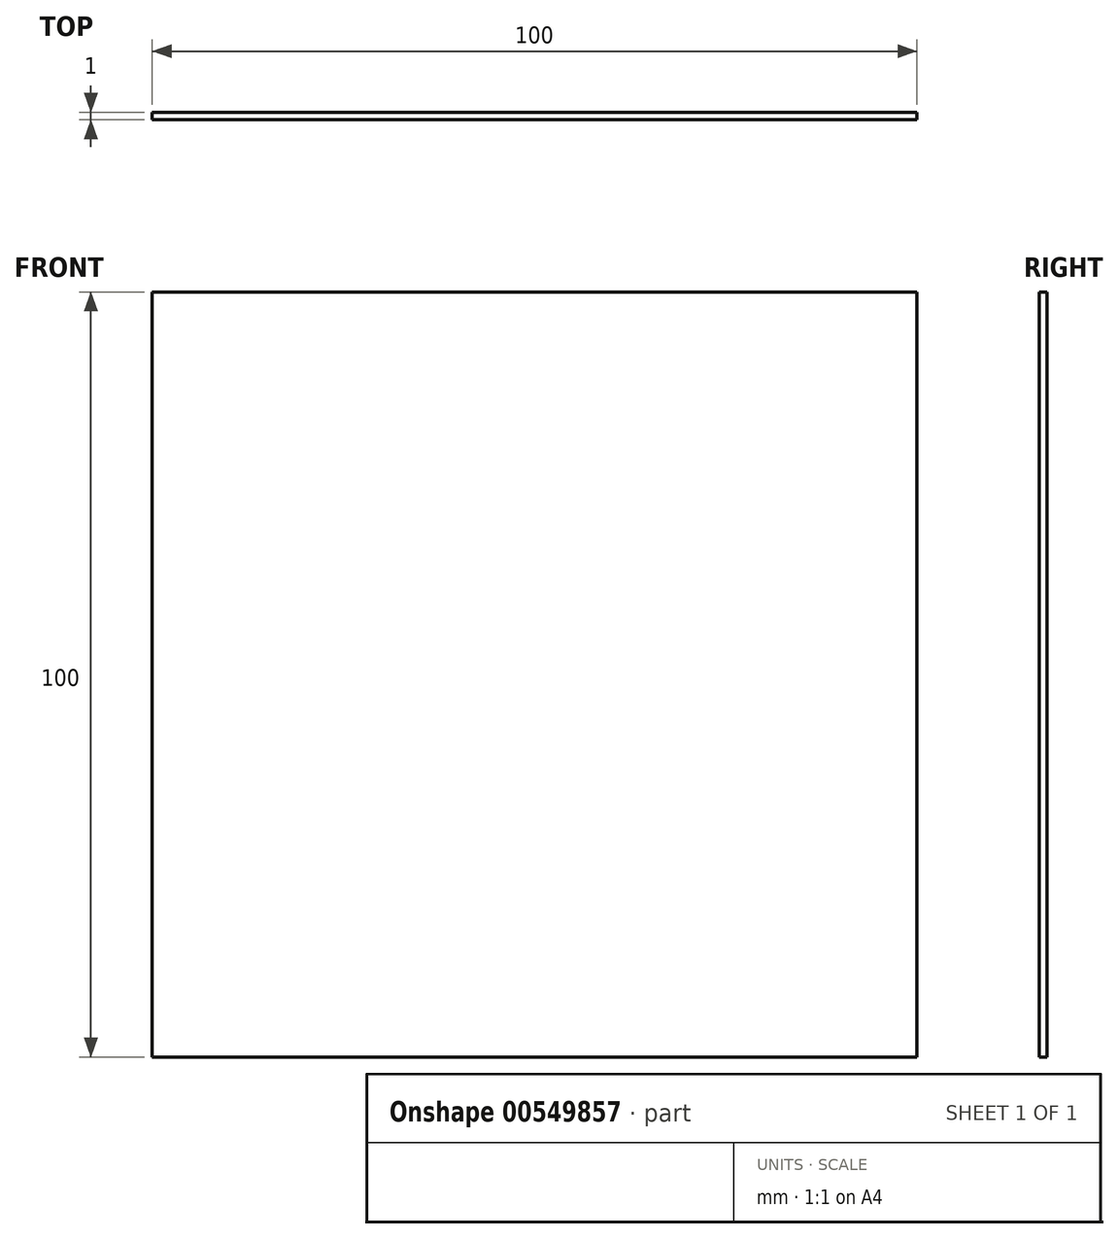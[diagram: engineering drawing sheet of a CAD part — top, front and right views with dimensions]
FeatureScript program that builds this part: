
annotation { "Feature Type Name" : "Feature", "Feature Type Description" : "" }
export const myFeature = defineFeature(function(context is Context, id is Id, definition is map)
    precondition{}
    {
        {
            var Q0;
            Q0=qCreatedBy(makeId("Front.planeOp"),FACE);
            var sketch = newSketch(context, id + "F0", { "sketchPlane" : qUnion([Q0])});
            skLineSegment(sketch, "E0.bottom", {"start": v(0, 0) * mm, "end": v(100, 0) * mm});
            skLineSegment(sketch, "E0.top", {"start": v(0, 100) * mm, "end": v(100, 100) * mm});
            skLineSegment(sketch, "E0.left", {"start": v(0, 0) * mm, "end": v(0, 100) * mm});
            skLineSegment(sketch, "E0.right", {"start": v(100, 0) * mm, "end": v(100, 100) * mm});
            skSolve(sketch);
        }
        {
            var Q0;
            Q0=makeQuery(id+"F0.imprint","IMPRINT",FACE,{"disambiguationData":[TD([[makeQuery(id+"F0.imprint","IMPRINT",EDGE,{"derivedFrom":sQuery(id+"F0.wireOp",EDGE,"E0.bottom")}),1.0]])]});
            extrude(context, id + "F1", {"entities" : qUnion([Q0]), "depth" : 1 * mm, "offsetDistance" : 25 * mm});
        }
    });
